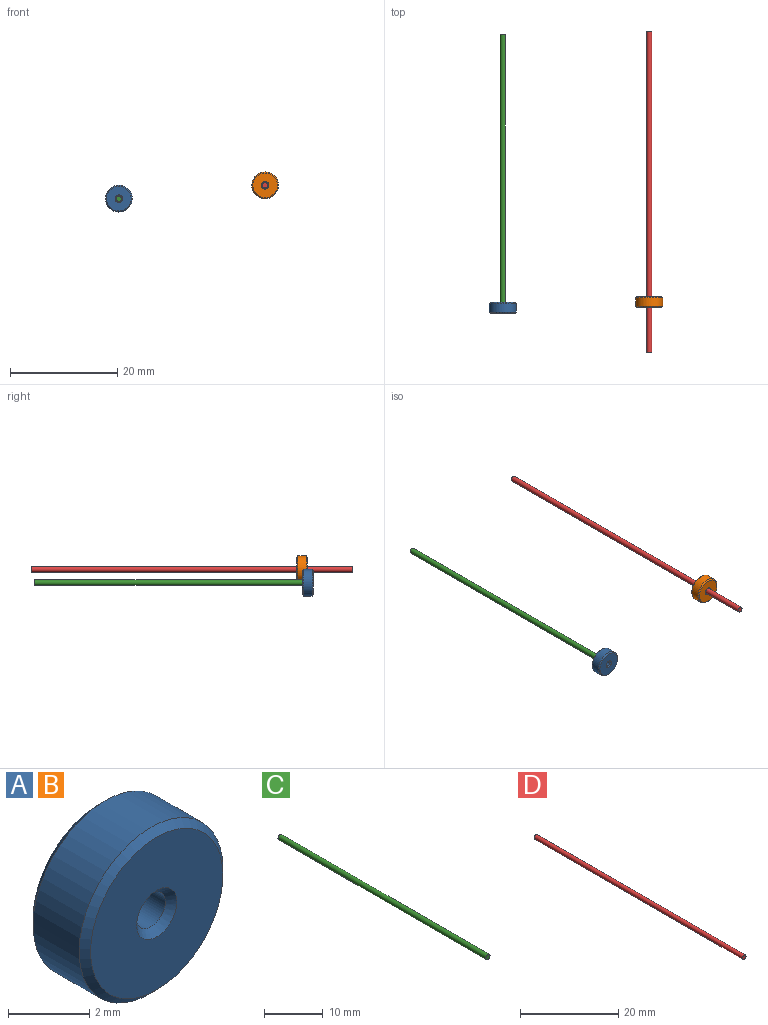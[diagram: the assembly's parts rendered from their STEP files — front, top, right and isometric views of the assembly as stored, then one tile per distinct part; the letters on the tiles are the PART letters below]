
ASSEMBLY  parts=4 mates=2
PART A: 8 faces, bbox 5x2x5 mm
  f0: cylinder r=0.5mm len=1.6mm, axis (0,1,0), area 5mm2, adj f5,f6
  f1: cylinder r=2.5mm len=5mm, axis (0,1,0), area 25.1mm2, adj f4,f7
  f2: plane 4.6x4.6mm, normal (0,-1,0), area 15.1mm2, adj f4,f5
  f3: plane 4.6x4.6mm, normal (0,1,0), area 15.1mm2, adj f6,f7
  f4: cone r=2.3mm half-angle=45deg, axis (0,1,0), area 4.3mm2, adj f1,f2
  f5: cone r=0.5mm half-angle=45deg, axis (0,-1,0), area 1.1mm2, adj f0,f2
  f6: cone r=0.7mm half-angle=45deg, axis (0,1,0), area 1.1mm2, adj f0,f3
  f7: cone r=2.5mm half-angle=45deg, axis (0,-1,0), area 4.3mm2, adj f1,f3
PART B: same geometry as A
PART C: 3 faces, bbox 1x50x1 mm
  f0: cylinder r=0.5mm len=50mm, axis (0,1,0), area 157.1mm2, adj f1,f2
  f1: plane 1x1mm, normal (0,-1,0), area 0.8mm2, adj f0
  f2: plane 1x1mm, normal (0,1,0), area 0.8mm2, adj f0
PART D: 3 faces, bbox 1x60x1 mm
  f0: cylinder r=0.5mm len=60mm, axis (0,1,0), area 188.5mm2, adj f1,f2
  f1: plane 1x1mm, normal (0,-1,0), area 0.8mm2, adj f0
  f2: plane 1x1mm, normal (0,1,0), area 0.8mm2, adj f0
PLACE A t=(0,-4.92,0)mm fixed
PLACE B rot(axis=(0,-1,0),159deg) t=(27.35,-3.87,2.49)mm
PLACE C rot(axis=(0,1,0),92.3deg) t=(0,-2.92,0)mm
PLACE D rot(axis=(0,-1,0),8.8deg) t=(-2.3,-2.3,-2.11)mm fixed
MATE revolute C.f0 <-> A.f1  axis (0,-1,0) through (0,-62.92,0)mm
MATE cylindrical B.f1 <-> D.f0  axis (0,1,0) through (27.35,-61.87,2.49)mm
